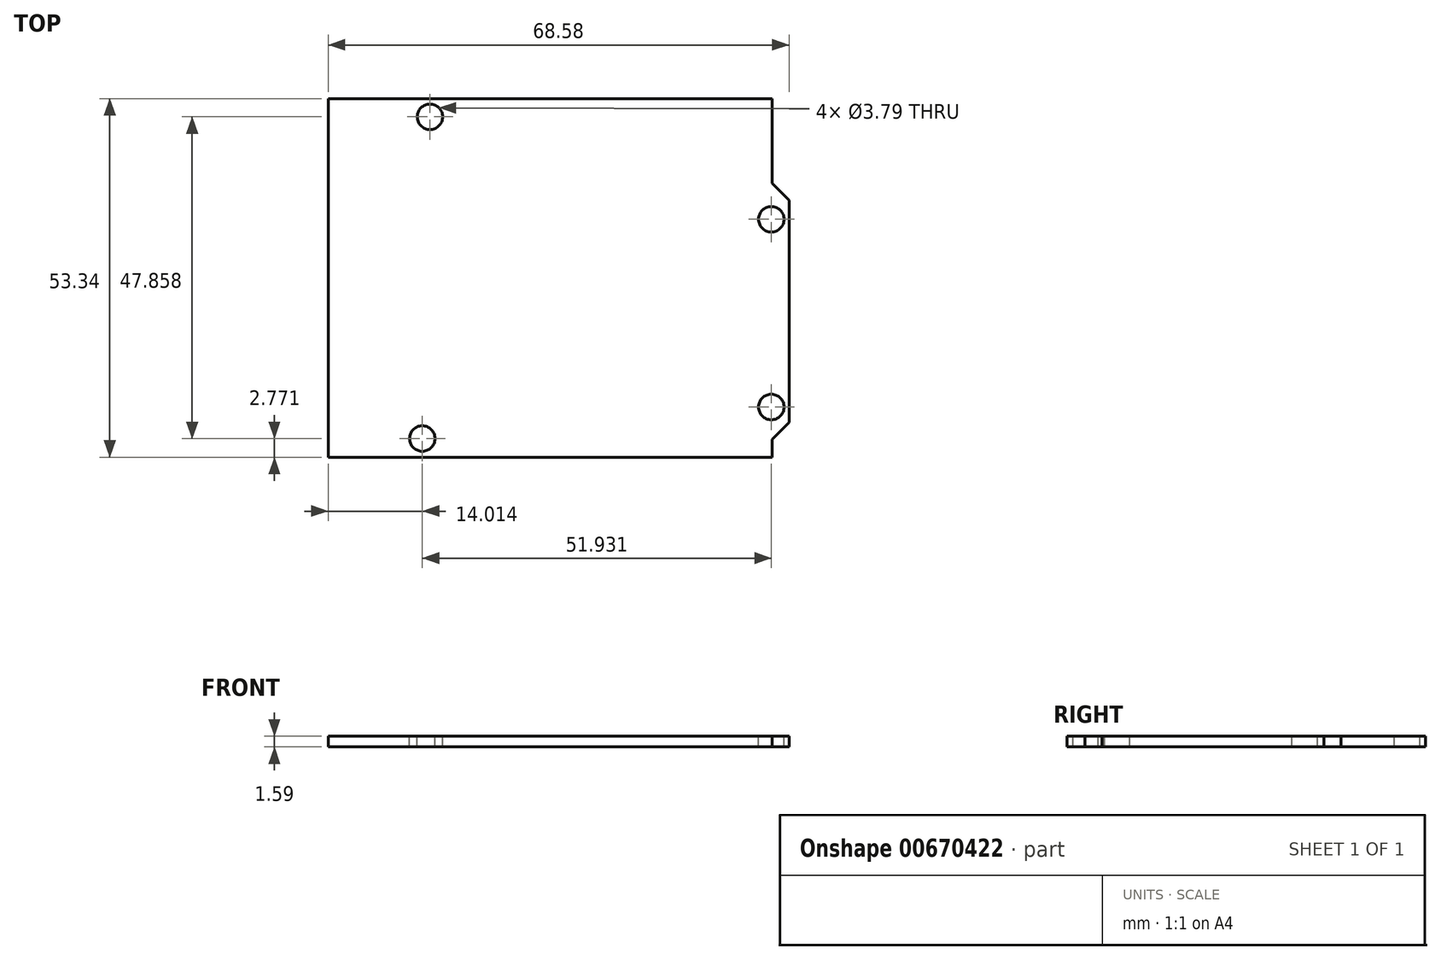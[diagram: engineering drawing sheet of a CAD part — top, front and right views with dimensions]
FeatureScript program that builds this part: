
annotation { "Feature Type Name" : "Feature", "Feature Type Description" : "" }
export const myFeature = defineFeature(function(context is Context, id is Id, definition is map)
    precondition{}
    {
        {
            var Q0;
            Q0=qCreatedBy(makeId("Top.planeOp"),FACE);
            var sketch = newSketch(context, id + "F0", { "sketchPlane" : qUnion([Q0])});
            skLineSegment(sketch, "E0", {"start": v(-33.02, 26.67) * mm, "end": v(33.02, 26.67) * mm});
            skLineSegment(sketch, "E1", {"start": v(33.02, 26.67) * mm, "end": v(33.02, 14.1) * mm});
            skLineSegment(sketch, "E2", {"start": v(33.02, -26.67) * mm, "end": v(-33.02, -26.67) * mm});
            skLineSegment(sketch, "E3", {"start": v(-33.02, -26.67) * mm, "end": v(-33.02, 26.67) * mm});
            skLineSegment(sketch, "E4", {"start": v(33.02, -24) * mm, "end": v(35.56, -21.46) * mm});
            skLineSegment(sketch, "E5", {"start": v(35.56, -21.46) * mm, "end": v(35.56, 11.56) * mm});
            skLineSegment(sketch, "E6", {"start": v(35.56, 11.56) * mm, "end": v(33.02, 14.1) * mm});
            skLineSegment(sketch, "E7", {"start": v(0, 0) * mm, "end": v(-33.02, 0) * mm, "construction": true});
            skPoint(sketch, "E8.end.orphan", {"position": v(0, 26.67) * mm});
            skLineSegment(sketch, "E9", {"start": v(0, 0) * mm, "end": v(0, 26.67) * mm, "construction": true});
            skLineSegment(sketch, "E10", {"start": v(33.02, -24) * mm, "end": v(33.02, -26.67) * mm});
            skSolve(sketch);
        }
        {
            var Q0;
            Q0=makeQuery(id+"F0.imprint","IMPRINT",FACE,{"disambiguationData":[TD([[makeQuery(id+"F0.imprint","IMPRINT",EDGE,{"derivedFrom":sQuery(id+"F0.wireOp",EDGE,"E0")}),-1.0]])]});
            extrude(context, id + "F1", {"entities" : qUnion([Q0]), "depth" : 1.59 * mm, "offsetDistance" : 25 * mm});
        }
        {
            var Q0;
            Q0=makeQuery(id+"F1.opExtrude","CAP_FACE",FACE,{"disambiguationData":[OSD([sQuery(id+"F0.wireOp",EDGE,"E0"),sQuery(id+"F0.wireOp",EDGE,"E1"),sQuery(id+"F0.wireOp",EDGE,"E2"),sQuery(id+"F0.wireOp",EDGE,"E3"),sQuery(id+"F0.wireOp",EDGE,"E4"),sQuery(id+"F0.wireOp",EDGE,"E5"),sQuery(id+"F0.wireOp",EDGE,"E6"),sQuery(id+"F0.wireOp",EDGE,"E10")])],"isStart":false});
            var sketch = newSketch(context, id + "F2", { "sketchPlane" : qUnion([Q0])});
            skCircle(sketch, "E11", {"center": v(-17.86, 23.96) * mm, "radius": 1.9 * mm});
            skCircle(sketch, "E12", {"center": v(32.93, 8.72) * mm, "radius": 1.9 * mm});
            skCircle(sketch, "E13", {"center": v(-19, -23.9) * mm, "radius": 1.9 * mm});
            skCircle(sketch, "E14", {"center": v(32.93, -19.2) * mm, "radius": 1.9 * mm});
            skSolve(sketch);
        }
        {
            var Q0;
            Q0=makeQuery(id+"F2.imprint","IMPRINT",FACE,{"disambiguationData":[TD([[makeQuery(id+"F2.imprint","IMPRINT",EDGE,{"derivedFrom":sQuery(id+"F2.wireOp",EDGE,"E13")}),1.0]])]});
            var Q1;
            Q1=makeQuery(id+"F2.imprint","IMPRINT",FACE,{"disambiguationData":[TD([[makeQuery(id+"F2.imprint","IMPRINT",EDGE,{"derivedFrom":sQuery(id+"F2.wireOp",EDGE,"E14")}),1.0]])]});
            var Q2;
            Q2=makeQuery(id+"F2.imprint","IMPRINT",FACE,{"disambiguationData":[TD([[makeQuery(id+"F2.imprint","IMPRINT",EDGE,{"derivedFrom":sQuery(id+"F2.wireOp",EDGE,"E12")}),1.0]])]});
            var Q3;
            Q3=makeQuery(id+"F2.imprint","IMPRINT",FACE,{"disambiguationData":[TD([[makeQuery(id+"F2.imprint","IMPRINT",EDGE,{"derivedFrom":sQuery(id+"F2.wireOp",EDGE,"E11")}),1.0]])]});
            extrude(context, id + "F3", {"entities" : qUnion([Q0, Q1, Q2, Q3]), "operationType" : NewBodyOperationType.REMOVE, "oppositeDirection" : true, "depth" : 25 * mm, "offsetDistance" : 25 * mm});
        }
    });
